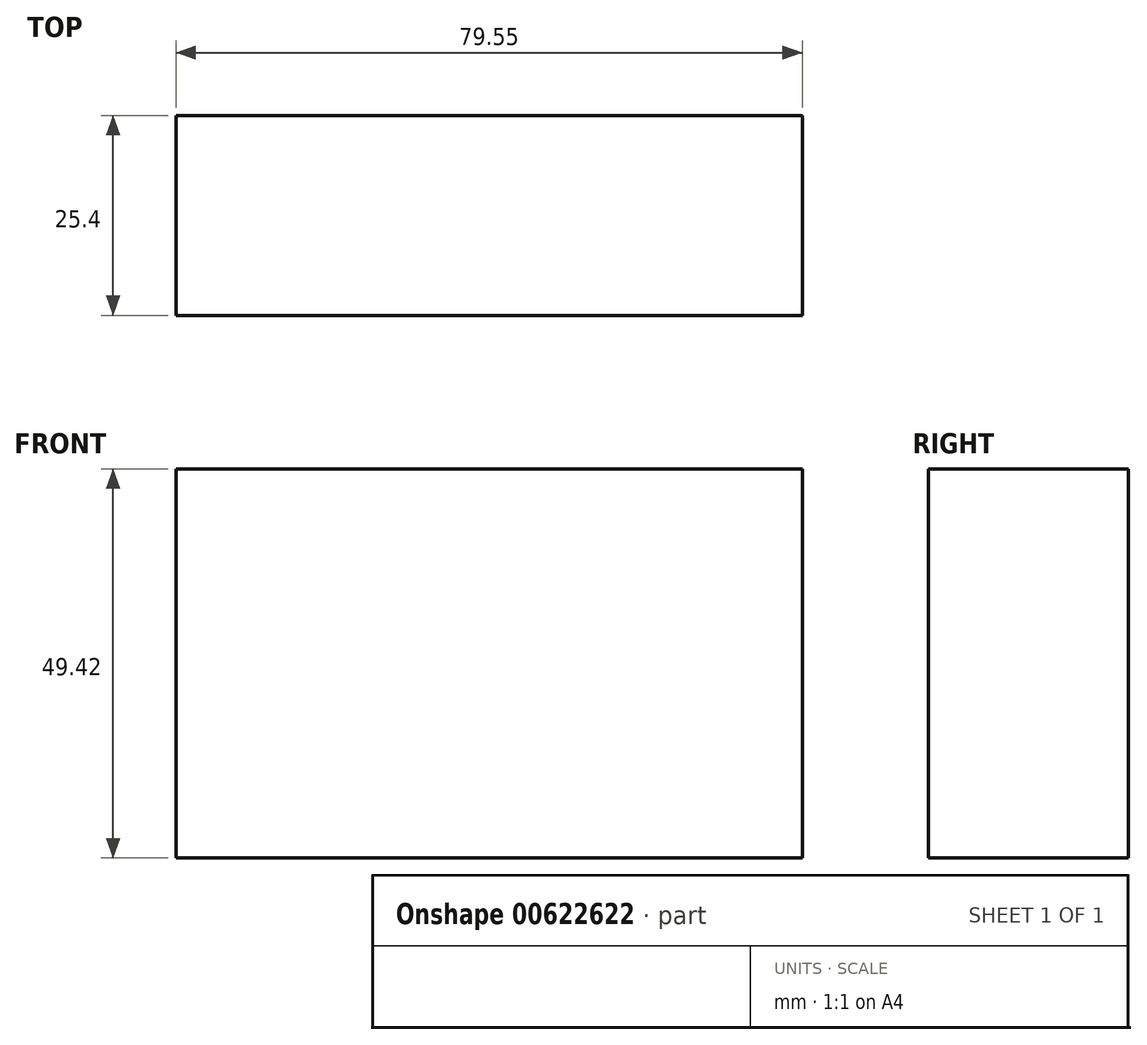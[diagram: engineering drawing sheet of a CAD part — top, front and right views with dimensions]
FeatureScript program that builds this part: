
annotation { "Feature Type Name" : "Feature", "Feature Type Description" : "" }
export const myFeature = defineFeature(function(context is Context, id is Id, definition is map)
    precondition{}
    {
        {
            var Q0;
            Q0=qCreatedBy(makeId("Front.planeOp"),FACE);
            var sketch = newSketch(context, id + "F0", { "sketchPlane" : qUnion([Q0])});
            skLineSegment(sketch, "E0.bottom", {"start": v(-38.36, 49.42) * mm, "end": v(41.19, 49.42) * mm});
            skLineSegment(sketch, "E0.top", {"start": v(-38.36, 0) * mm, "end": v(41.19, 0) * mm});
            skLineSegment(sketch, "E0.left", {"start": v(-38.36, 49.42) * mm, "end": v(-38.36, 0) * mm});
            skLineSegment(sketch, "E0.right", {"start": v(41.19, 49.42) * mm, "end": v(41.19, 0) * mm});
            skSolve(sketch);
        }
        {
            var Q0;
            Q0 = qSketchRegion(id + "F0", true);
            extrude(context, id + "F1", {"entities" : qUnion([Q0]), "depth" : 25.4 * mm, "offsetDistance" : 25.4 * mm});
        }
    });
